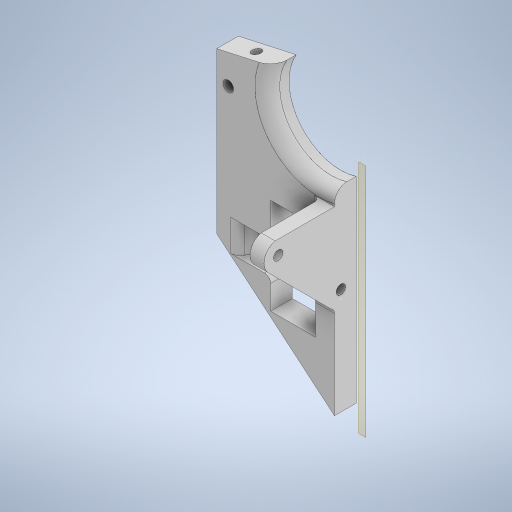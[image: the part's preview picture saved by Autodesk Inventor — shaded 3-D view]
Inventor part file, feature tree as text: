
AUTODESK INVENTOR PART (.ipt)
format: ipt  version: 2023 (Build 270158000, 158)  size: 457,728 bytes
history: native  units: in
note: dims shown in document units (in); Inventor stores cm internally (conversion verified against a paired STEP export)
features: sketch x27, other x6, extrude x1, projected_geometry x1
ambient origin geometry x8: Origin, YZ Plane, XZ Plane, XY Plane, X Axis, Y Axis, Z Axis, Center Point
bodies: Body1 (feature_tree)
feature tree (35):
  other  "sciana PRE 2.0.ipt"
  extrude  "Wyciągnięcie proste1"  Depth=0.3937in
  other  "Bryła1::sciana PRE 2.0.ipt"
  other  "Bryła wyprowadzona1"
  sketch  "Szkic1"
  sketch  "Szkic2"
  sketch  "Szkic3"
  sketch  "Szkic4"
  sketch  "Szkic5"
  sketch  "Szkic6"
  sketch  "Szkic7"
  sketch  "Szkic8"
  sketch  "Szkic9"
  sketch  "Szkic10"
  sketch  "Szkic11"
  sketch  "Szkic12"
  sketch  "Szkic13"
  sketch  "Szkic14"
  sketch  "Szkic15"
  sketch  "Szkic16"
  sketch  "Szkic17"
  sketch  "Szkic18"
  sketch  "Szkic19"
  sketch  "Szkic20"
  sketch  "Szkic21"
  sketch  "Szkic22"
  sketch  "Szkic23"
  sketch  "Szkic24"
  sketch  "Szkic25"
  sketch  "Szkic26"
  other  "Płaszczyzna konstrukcyjna1"
  other  "Płaszczyzna konstrukcyjna2"
  sketch  "Szkic27"
  projected_geometry  "Pętla rzutowana1"
  other  "Bryła1"
